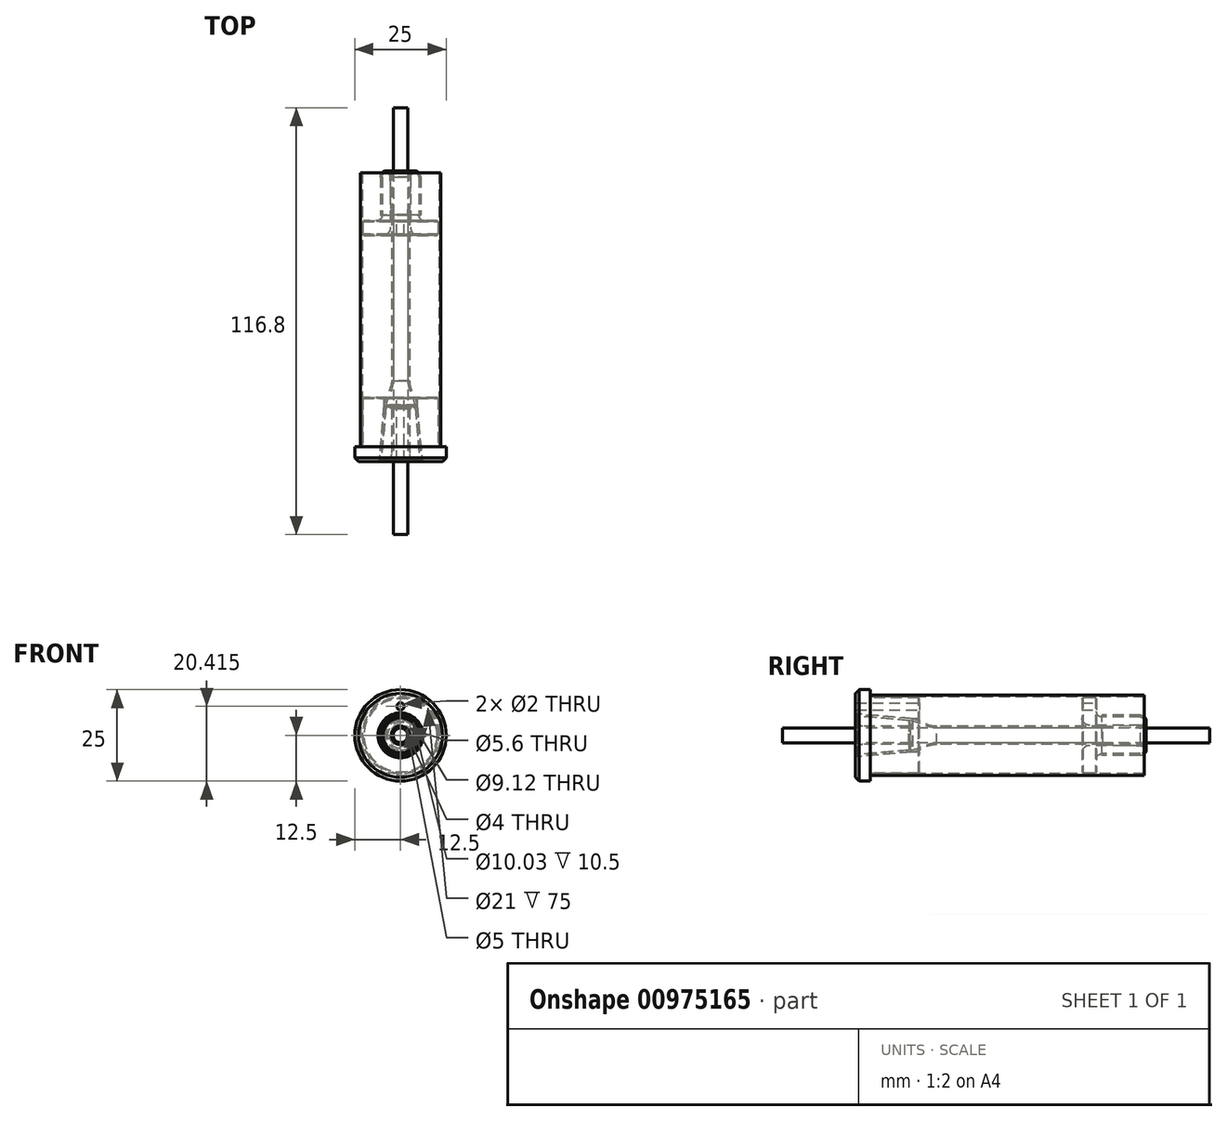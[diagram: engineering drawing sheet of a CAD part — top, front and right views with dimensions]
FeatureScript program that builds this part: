
annotation { "Feature Type Name" : "Feature", "Feature Type Description" : "" }
export const myFeature = defineFeature(function(context is Context, id is Id, definition is map)
    precondition{}
    {
        {
            var Q0;
            Q0=qCreatedBy(makeId("Right.planeOp"),FACE);
            var sketch = newSketch(context, id + "F0", { "sketchPlane" : qUnion([Q0])});
            skLineSegment(sketch, "E0.bottom", {"start": v(-20, 0) * mm, "end": v(96.8, 0) * mm});
            skLineSegment(sketch, "E0.top", {"start": v(-20, 2) * mm, "end": v(96.8, 2) * mm});
            skLineSegment(sketch, "E0.left", {"start": v(-20, 0) * mm, "end": v(-20, 2) * mm});
            skLineSegment(sketch, "E0.right", {"start": v(96.8, 0) * mm, "end": v(96.8, 2) * mm});
            skLineSegment(sketch, "E1", {"start": v(0, 2.5) * mm, "end": v(15, 2.5) * mm});
            skLineSegment(sketch, "E2", {"start": v(15, 2.5) * mm, "end": v(15, 4) * mm});
            skLineSegment(sketch, "E3", {"start": v(15, 4) * mm, "end": v(0, 5.31) * mm});
            skLineSegment(sketch, "E4", {"start": v(0, 5.31) * mm, "end": v(0, 2.5) * mm});
            skLineSegment(sketch, "E5", {"start": v(0, 5.91) * mm, "end": v(15.5, 4.56) * mm});
            skLineSegment(sketch, "E6", {"start": v(17.5, 4.56) * mm, "end": v(17.5, 10.3) * mm});
            skLineSegment(sketch, "E7", {"start": v(17.5, 10.3) * mm, "end": v(4, 10.3) * mm});
            skLineSegment(sketch, "E8", {"start": v(4, 10.3) * mm, "end": v(4, 12.5) * mm});
            skLineSegment(sketch, "E9", {"start": v(4, 12.5) * mm, "end": v(0, 12.5) * mm});
            skLineSegment(sketch, "E10", {"start": v(0, 12.5) * mm, "end": v(0, 5.91) * mm});
            skLineSegment(sketch, "E11", {"start": v(15.5, 4.56) * mm, "end": v(17.5, 4.56) * mm});
            skPoint(sketch, "E12", {"position": v(4, 5.56) * mm});
            skLineSegment(sketch, "E13.bottom", {"start": v(17.5, 6.91) * mm, "end": v(0, 6.91) * mm, "construction": true});
            skLineSegment(sketch, "E13.top", {"start": v(17.5, 8.91) * mm, "end": v(0, 8.91) * mm, "construction": true});
            skLineSegment(sketch, "E13.left", {"start": v(17.5, 6.91) * mm, "end": v(17.5, 8.91) * mm, "construction": true});
            skLineSegment(sketch, "E13.right", {"start": v(0, 6.91) * mm, "end": v(0, 8.91) * mm, "construction": true});
            skSolve(sketch);
        }
        {
            var Q0;
            Q0=qCreatedBy(makeId("Right.planeOp"),FACE);
            var sketch = newSketch(context, id + "F1", { "sketchPlane" : qUnion([Q0])});
            skLineSegment(sketch, "E14.0", {"start": v(17.5, 8.91) * mm, "end": v(0, 8.91) * mm});
            skLineSegment(sketch, "E14.1", {"start": v(17.5, 6.91) * mm, "end": v(0, 6.91) * mm});
            skLineSegment(sketch, "E15", {"start": v(0, 8.91) * mm, "end": v(0, 6.91) * mm});
            skLineSegment(sketch, "E16", {"start": v(17.5, 8.91) * mm, "end": v(17.5, 6.91) * mm});
            skLineSegment(sketch, "E17", {"start": v(0, 7.91) * mm, "end": v(17.5, 7.91) * mm});
            skSolve(sketch);
        }
        {
            var Q0;
            Q0=qCreatedBy(makeId("Right.planeOp"),FACE);
            var sketch = newSketch(context, id + "F2", { "sketchPlane" : qUnion([Q0])});
            skLineSegment(sketch, "E18.0", {"start": v(-20, 2) * mm, "end": v(96.8, 2) * mm, "construction": true});
            skLineSegment(sketch, "E18.1", {"start": v(-20, 0) * mm, "end": v(96.8, 0) * mm, "construction": true});
            skPoint(sketch, "E19.0", {"position": v(17.5, 10.3) * mm});
            skPoint(sketch, "E19.1", {"position": v(17.5, 8.91) * mm});
            skPoint(sketch, "E19.2", {"position": v(17.5, 4.56) * mm});
            skPoint(sketch, "E20.0", {"position": v(17.5, 6.91) * mm});
            skLineSegment(sketch, "E21", {"start": v(61.9, 10.3) * mm, "end": v(61.9, 2.8) * mm});
            skLineSegment(sketch, "E22", {"start": v(61.9, 2.8) * mm, "end": v(77.9, 2.8) * mm});
            skLineSegment(sketch, "E23", {"start": v(61.9, 10.3) * mm, "end": v(65.9, 10.3) * mm});
            skLineSegment(sketch, "E24", {"start": v(65.9, 10.3) * mm, "end": v(65.9, 6.51) * mm});
            skLineSegment(sketch, "E25", {"start": v(67.4, 5.01) * mm, "end": v(77.9, 5.01) * mm});
            skLineSegment(sketch, "E26", {"start": v(77.9, 5.01) * mm, "end": v(77.9, 2.8) * mm, "construction": true});
            skArc(sketch, "E27", {"start": v(77.9, 5.01) * mm, "mid": v(79, 3.9) * mm, "end": v(77.9, 2.8) * mm});
            skPoint(sketch, "E28.0", {"position": v(15, 2.5) * mm});
            skLineSegment(sketch, "E29", {"start": v(61.9, 8.91) * mm, "end": v(65.9, 8.91) * mm});
            skLineSegment(sketch, "E30", {"start": v(61.9, 6.91) * mm, "end": v(65.9, 6.91) * mm, "construction": true});
            skLineSegment(sketch, "E31.bottom", {"start": v(4, 11) * mm, "end": v(79, 11) * mm});
            skLineSegment(sketch, "E31.top", {"start": v(4, 10.5) * mm, "end": v(79, 10.5) * mm});
            skLineSegment(sketch, "E31.left", {"start": v(4, 11) * mm, "end": v(4, 10.5) * mm});
            skLineSegment(sketch, "E31.right", {"start": v(79, 11) * mm, "end": v(79, 10.5) * mm});
            skPoint(sketch, "E32.0", {"position": v(4, 12.5) * mm});
            skLineSegment(sketch, "E33", {"start": v(61.9, 7.91) * mm, "end": v(65.9, 7.91) * mm});
            skPoint(sketch, "E34.visualSharp", {"position": v(65.9, 5.01) * mm});
            skArc(sketch, "E34.filletArc", {"start": v(65.9, 6.51) * mm, "mid": v(66.33, 5.45) * mm, "end": v(67.4, 5.01) * mm});
            skPoint(sketch, "E35", {"position": v(79, 3.9) * mm});
            skSolve(sketch);
        }
        {
            var Q0;
            Q0=makeQuery(id+"F0.imprint","IMPRINT",FACE,{"disambiguationData":[TD([[makeQuery(id+"F0.imprint","IMPRINT",EDGE,{"derivedFrom":sQuery(id+"F0.wireOp",EDGE,"E0.bottom")}),1.0]])]});
            var Q1;
            Q1=makeQuery(id+"F0.imprint","IMPRINT",FACE,{"disambiguationData":[TD([[makeQuery(id+"F0.imprint","IMPRINT",EDGE,{"derivedFrom":sQuery(id+"F0.wireOp",EDGE,"E1")}),1.0]])]});
            var Q2;
            Q2=makeQuery(id+"F0.imprint","IMPRINT",FACE,{"disambiguationData":[TD([[makeQuery(id+"F0.imprint","IMPRINT",EDGE,{"derivedFrom":sQuery(id+"F0.wireOp",EDGE,"E5")}),1.0]])]});
            var Q3;
            Q3=sQuery(id+"F0.wireOp",EDGE,"E0.bottom");
            revolve(context, id + "F3", {"surfaceOperationType" : NewSurfaceOperationType.NEW, "entities" : qUnion([Q0, Q1, Q2]), "axis" : qUnion([Q3]), "revolveType" : RevolveType.FULL});
        }
        {
            var Q0;
            {var subQ0=sQuery(id+"F1.wireOp",EDGE,"E14.0");Q0=makeQuery(id+"F1.imprint","IMPRINT",FACE,{"disambiguationData":[TD([[makeQuery(id+"F1.imprint","IMPRINT",EDGE,{"derivedFrom":subQ0}),1.0]])]});}
            var Q1;
            Q1=sQuery(id+"F1.wireOp",EDGE,"E17");
            revolve(context, id + "F4", {"operationType" : NewBodyOperationType.REMOVE, "surfaceOperationType" : NewSurfaceOperationType.NEW, "entities" : qUnion([Q0]), "axis" : qUnion([Q1]), "revolveType" : RevolveType.FULL, "oppositeDirection" : true});
        }
        {
            var Q0;
            Q0=makeQuery(id+"F3.opRevolve","SWEPT_EDGE",EDGE,{"disambiguationData":[OSD([sQuery(id+"F0.wireOp",EDGE,"E1"),sQuery(id+"F0.wireOp",EDGE,"E4")])]});
            fillet(context, id + "F5", {"entities" : qUnion([Q0]), "radius" : 2 * mm, "tangentPropagation" : true, "allowEdgeOverflow" : false});
        }
        {
            var Q0;
            Q0=makeQuery(id+"F3.opRevolve","SWEPT_EDGE",EDGE,{"disambiguationData":[OSD([sQuery(id+"F0.wireOp",EDGE,"E3"),sQuery(id+"F0.wireOp",EDGE,"E4")])]});
            var Q1;
            Q1=makeQuery(id+"F3.opRevolve","SWEPT_EDGE",EDGE,{"disambiguationData":[OSD([sQuery(id+"F0.wireOp",EDGE,"E2"),sQuery(id+"F0.wireOp",EDGE,"E3")])]});
            var Q2;
            Q2=makeQuery(id+"F3.opRevolve","SWEPT_EDGE",EDGE,{"disambiguationData":[OSD([sQuery(id+"F0.wireOp",EDGE,"E1"),sQuery(id+"F0.wireOp",EDGE,"E2")])]});
            chamfer(context, id + "F6", {"entities" : qUnion([Q0, Q1, Q2]), "width" : .5 * mm, "tangentPropagation" : true});
        }
        {
            var Q0;
            Q0=makeQuery(id+"F3.opRevolve","SWEPT_EDGE",EDGE,{"disambiguationData":[OSD([sQuery(id+"F0.wireOp",EDGE,"E9"),sQuery(id+"F0.wireOp",EDGE,"E10")])]});
            chamfer(context, id + "F7", {"entities" : qUnion([Q0]), "width" : 1 * mm, "tangentPropagation" : true});
        }
        {
            var Q0;
            Q0=makeQuery(id+"F3.opRevolve","SWEPT_EDGE",EDGE,{"disambiguationData":[OSD([sQuery(id+"F0.wireOp",EDGE,"E5"),sQuery(id+"F0.wireOp",EDGE,"E10")])]});
            var Q1;
            Q1=makeQuery(id+"F3.opRevolve","SWEPT_EDGE",EDGE,{"disambiguationData":[OSD([sQuery(id+"F0.wireOp",EDGE,"E6"),sQuery(id+"F0.wireOp",EDGE,"E7")])]});
            var Q2;
            Q2=makeQuery(id+"F3.opRevolve","SWEPT_EDGE",EDGE,{"disambiguationData":[OSD([sQuery(id+"F0.wireOp",EDGE,"E6"),sQuery(id+"F0.wireOp",EDGE,"E11")])]});
            var Q3;
            Q3=makeQuery(id+"F3.opRevolve","SWEPT_EDGE",EDGE,{"disambiguationData":[OSD([sQuery(id+"F0.wireOp",EDGE,"E5"),sQuery(id+"F0.wireOp",EDGE,"E11")])]});
            var Q4;
            Q4=makeQuery(id+"F4.boolean.opBoolean","COPY",EDGE,{"derivedFrom":makeQuery(id+"F4.opRevolve","SWEPT_EDGE",EDGE,{"disambiguationData":[OSD([sQuery(id+"F1.wireOp",EDGE,"E14.0"),sQuery(id+"F1.wireOp",EDGE,"E15")])]})});
            var Q5;
            Q5=makeQuery(id+"F4.boolean.opBoolean","COPY",EDGE,{"derivedFrom":makeQuery(id+"F4.opRevolve","SWEPT_EDGE",EDGE,{"disambiguationData":[OSD([sQuery(id+"F1.wireOp",EDGE,"E14.0"),sQuery(id+"F1.wireOp",EDGE,"E16")])]})});
            var Q6;
            Q6=makeQuery(id+"Fe6vTQibgBrM3nR_3.1.F4.boolean.opBoolean","COPY",EDGE,{"derivedFrom":makeQuery(id+"Fe6vTQibgBrM3nR_3.1.F4.opRevolve","SWEPT_EDGE",EDGE,{"disambiguationData":[OSD([sQuery(id+"F1.wireOp",EDGE,"E14.0"),sQuery(id+"F1.wireOp",EDGE,"E16")])]})});
            var Q7;
            Q7=makeQuery(id+"Fe6vTQibgBrM3nR_3.1.F4.boolean.opBoolean","COPY",EDGE,{"derivedFrom":makeQuery(id+"Fe6vTQibgBrM3nR_3.1.F4.opRevolve","SWEPT_EDGE",EDGE,{"disambiguationData":[OSD([sQuery(id+"F1.wireOp",EDGE,"E14.0"),sQuery(id+"F1.wireOp",EDGE,"E15")])]})});
            chamfer(context, id + "F8", {"entities" : qUnion([Q0, Q1, Q2, Q3, Q4, Q5, Q6, Q7]), "width" : .25 * mm, "tangentPropagation" : true});
        }
        {
            var Q0;
            Q0=makeQuery(id+"F2.imprint","IMPRINT",FACE,{"disambiguationData":[TD([[makeQuery(id+"F2.imprint","IMPRINT",EDGE,{"derivedFrom":sQuery(id+"F2.wireOp",EDGE,"E31.bottom")}),-1.0]])]});
            var Q1;
            {var subQ0=sQuery(id+"F2.wireOp",EDGE,"E23");Q1=makeQuery(id+"F2.imprint","IMPRINT",FACE,{"disambiguationData":[TD([[makeQuery(id+"F2.imprint","IMPRINT",EDGE,{"derivedFrom":subQ0}),-1.0]])]});}
            var Q2;
            {var subQ0=sQuery(id+"F2.wireOp",EDGE,"E29");Q2=makeQuery(id+"F2.imprint","IMPRINT",FACE,{"disambiguationData":[TD([[makeQuery(id+"F2.imprint","IMPRINT",EDGE,{"derivedFrom":subQ0}),-1.0]])]});}
            var Q3;
            {var subQ0=sQuery(id+"F2.wireOp",EDGE,"E22");Q3=makeQuery(id+"F2.imprint","IMPRINT",FACE,{"disambiguationData":[TD([[makeQuery(id+"F2.imprint","IMPRINT",EDGE,{"derivedFrom":subQ0}),1.0]])]});}
            var Q4;
            Q4=sQuery(id+"F0.wireOp",EDGE,"E0.bottom");
            revolve(context, id + "F9", {"surfaceOperationType" : NewSurfaceOperationType.NEW, "entities" : qUnion([Q0, Q1, Q2, Q3]), "axis" : qUnion([Q4]), "revolveType" : RevolveType.FULL});
        }
        {
            var Q0;
            {var subQ0=sQuery(id+"F2.wireOp",EDGE,"E29");Q0=makeQuery(id+"F2.imprint","IMPRINT",FACE,{"disambiguationData":[TD([[makeQuery(id+"F2.imprint","IMPRINT",EDGE,{"derivedFrom":subQ0}),-1.0]])]});}
            var Q1;
            Q1=sQuery(id+"F2.wireOp",EDGE,"E33");
            revolve(context, id + "F10", {"operationType" : NewBodyOperationType.REMOVE, "surfaceOperationType" : NewSurfaceOperationType.NEW, "entities" : qUnion([Q0]), "axis" : qUnion([Q1]), "revolveType" : RevolveType.FULL, "oppositeDirection" : true});
        }
        {
            var Q0;
            Q0=makeQuery(id+"F9.opRevolve","SWEPT_EDGE",EDGE,{"disambiguationData":[OSD([sQuery(id+"F2.wireOp",EDGE,"E21"),sQuery(id+"F2.wireOp",EDGE,"E22")])]});
            fillet(context, id + "F11", {"entities" : qUnion([Q0]), "radius" : 2 * mm, "tangentPropagation" : true, "allowEdgeOverflow" : false});
        }
        {
            var Q0;
            Q0=makeQuery(id+"F9.opRevolve","SWEPT_EDGE",EDGE,{"disambiguationData":[OSD([sQuery(id+"F2.wireOp",EDGE,"E21"),sQuery(id+"F2.wireOp",EDGE,"E23")])]});
            var Q1;
            Q1=makeQuery(id+"F10.boolean.opBoolean","COPY",EDGE,{"derivedFrom":makeQuery(id+"F10.opRevolve","SWEPT_EDGE",EDGE,{"disambiguationData":[OSD([sQuery(id+"F2.wireOp",EDGE,"E21"),sQuery(id+"F2.wireOp",EDGE,"E29")])]})});
            var Q2;
            Q2=makeQuery(id+"F10.boolean.opBoolean","COPY",EDGE,{"derivedFrom":makeQuery(id+"F10.opRevolve","SWEPT_EDGE",EDGE,{"disambiguationData":[OSD([sQuery(id+"F2.wireOp",EDGE,"E24"),sQuery(id+"F2.wireOp",EDGE,"E29")])]})});
            var Q3;
            Q3=makeQuery(id+"F9.opRevolve","SWEPT_EDGE",EDGE,{"disambiguationData":[OSD([sQuery(id+"F2.wireOp",EDGE,"E23"),sQuery(id+"F2.wireOp",EDGE,"E24")])]});
            var Q4;
            Q4=makeQuery(id+"FOWtexT9L5pqyQL_5.1.F10.boolean.opBoolean","COPY",EDGE,{"derivedFrom":makeQuery(id+"FOWtexT9L5pqyQL_5.1.F10.opRevolve","SWEPT_EDGE",EDGE,{"disambiguationData":[OSD([sQuery(id+"F2.wireOp",EDGE,"E21"),sQuery(id+"F2.wireOp",EDGE,"E29")])]})});
            var Q5;
            Q5=makeQuery(id+"FOWtexT9L5pqyQL_5.1.F10.boolean.opBoolean","COPY",EDGE,{"derivedFrom":makeQuery(id+"FOWtexT9L5pqyQL_5.1.F10.opRevolve","SWEPT_EDGE",EDGE,{"disambiguationData":[OSD([sQuery(id+"F2.wireOp",EDGE,"E24"),sQuery(id+"F2.wireOp",EDGE,"E29")])]})});
            chamfer(context, id + "F12", {"entities" : qUnion([Q0, Q1, Q2, Q3, Q4, Q5]), "width" : .3 * mm, "tangentPropagation" : true});
        }
        {
            var Q0;
            Q0=qCreatedBy(makeId("Right.planeOp"),FACE);
            var sketch = newSketch(context, id + "F13", { "sketchPlane" : qUnion([Q0])});
            skLineSegment(sketch, "E36.0", {"start": v(15, 4) * mm, "end": v(0, 5.31) * mm});
            skLineSegment(sketch, "E37.0", {"start": v(61.9, 2.8) * mm, "end": v(77.9, 2.8) * mm, "construction": true});
            skArc(sketch, "E38.0", {"start": v(77.9, 5.01) * mm, "mid": v(79, 3.9) * mm, "end": v(77.9, 2.8) * mm});
            skLineSegment(sketch, "E39.0", {"start": v(67.4, 5.01) * mm, "end": v(77.9, 5.01) * mm});
            skLineSegment(sketch, "E40.0", {"start": v(22.12, 2) * mm, "end": v(67.6, 2) * mm});
            skFitSpline(sketch, "E41", {"points": [v(15, 4) * mm, v(22.12, 2) * mm], "startDerivative": vector(6.8, -0.6) * mm, "endDerivative": vector(7.82, 0) * mm});
            skPoint(sketch, "E42.orphan", {"position": v(-20, 2) * mm});
            skLineSegment(sketch, "E43.0", {"start": v(15.04, 4.5) * mm, "end": v(0, 5.81) * mm});
            skFitSpline(sketch, "E43.1", {"points": [v(15.04, 4.5) * mm, v(15.67, 4.44) * mm, v(16.88, 4.12) * mm, v(18.63, 3.38) * mm, v(20.36, 2.7) * mm, v(21.53, 2.5) * mm, v(22.12, 2.5) * mm]});
            skLineSegment(sketch, "E43.2", {"start": v(22.12, 2.5) * mm, "end": v(67.6, 2.5) * mm});
            skLineSegment(sketch, "E44", {"start": v(0, 5.31) * mm, "end": v(0, 5.81) * mm});
            skLineSegment(sketch, "E45", {"start": v(67.6, 2.5) * mm, "end": v(77.9, 2.8) * mm});
            skLineSegment(sketch, "E46", {"start": v(67.6, 2) * mm, "end": v(77.9, 2.3) * mm});
            skArc(sketch, "E47.0", {"start": v(77.9, 5.51) * mm, "mid": v(79.5, 3.9) * mm, "end": v(77.9, 2.3) * mm});
            skLineSegment(sketch, "E47.1", {"start": v(67.4, 5.51) * mm, "end": v(77.9, 5.51) * mm});
            skLineSegment(sketch, "E48", {"start": v(67.4, 5.51) * mm, "end": v(67.4, 5.01) * mm});
            skPoint(sketch, "E49.orphan", {"position": v(96.8, 2) * mm});
            skLineSegment(sketch, "E50.0", {"start": v(-20, 0) * mm, "end": v(96.8, 0) * mm, "construction": true});
            skSolve(sketch);
        }
        {
            var Q0;
            Q0=makeQuery(id+"F13.imprint","IMPRINT",FACE,{"disambiguationData":[TD([[makeQuery(id+"F13.imprint","IMPRINT",EDGE,{"derivedFrom":sQuery(id+"F13.wireOp",EDGE,"E36.0")}),-1.0]])]});
            var Q1;
            Q1=sQuery(id+"F13.wireOp",EDGE,"E50.0");
            revolve(context, id + "F14", {"surfaceOperationType" : NewSurfaceOperationType.NEW, "entities" : qUnion([Q0]), "axis" : qUnion([Q1]), "revolveType" : RevolveType.FULL});
        }
    });
